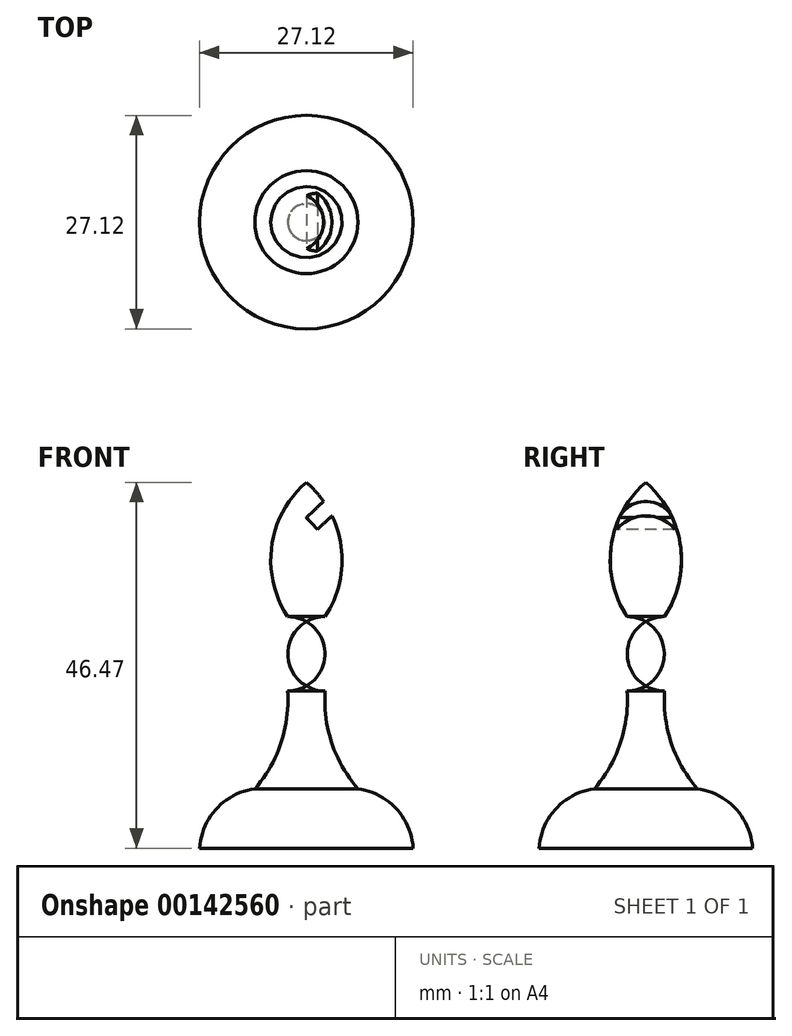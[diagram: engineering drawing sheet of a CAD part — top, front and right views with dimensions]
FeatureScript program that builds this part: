
annotation { "Feature Type Name" : "Feature", "Feature Type Description" : "" }
export const myFeature = defineFeature(function(context is Context, id is Id, definition is map)
    precondition{}
    {
        {
            var Q0;
            Q0=qCreatedBy(makeId("Front.planeOp"),FACE);
            var sketch = newSketch(context, id + "F0", { "sketchPlane" : qUnion([Q0])});
            skArc(sketch, "E0", {"start": v(13.56, 0) * mm, "mid": v(11.4, 5.02) * mm, "end": v(6.54, 7.54) * mm});
            skArc(sketch, "E1", {"start": v(2.38, 19.95) * mm, "mid": v(3.23, 13.33) * mm, "end": v(6.54, 7.54) * mm});
            skArc(sketch, "E2", {"start": v(2.38, 19.95) * mm, "mid": v(7.12, 24.69) * mm, "end": v(2.38, 29.42) * mm});
            skArc(sketch, "E3", {"start": v(2.38, 29.42) * mm, "mid": v(4.4, 38.4) * mm, "end": v(0, 46.47) * mm});
            skLineSegment(sketch, "E4", {"start": v(0, 46.47) * mm, "end": v(0, 0) * mm});
            skArc(sketch, "E5.MirrorCS", {"start": v(-2.38, 29.42) * mm, "mid": v(-4.4, 38.4) * mm, "end": v(0, 46.47) * mm});
            skArc(sketch, "E6.MirrorCS", {"start": v(-2.38, 19.95) * mm, "mid": v(-7.12, 24.69) * mm, "end": v(-2.38, 29.42) * mm});
            skArc(sketch, "E7.MirrorCS", {"start": v(-2.38, 19.95) * mm, "mid": v(-3.23, 13.33) * mm, "end": v(-6.54, 7.54) * mm});
            skArc(sketch, "E8.MirrorCS", {"start": v(-13.56, 0) * mm, "mid": v(-11.4, 5.02) * mm, "end": v(-6.54, 7.54) * mm});
            skLineSegment(sketch, "E9", {"start": v(13.56, 0) * mm, "end": v(-13.56, 0) * mm});
            skPoint(sketch, "E10.endSnap0", {"position": v(4.4, 38.4) * mm});
            skSolve(sketch);
        }
        {
            var Q0;
            Q0=qCreatedBy(makeId("Front.planeOp"),FACE);
            var sketch = newSketch(context, id + "F1", { "sketchPlane" : qUnion([Q0])});
            skLineSegment(sketch, "E11", {"start": v(4.87, 43.76) * mm, "end": v(1.42, 40.5) * mm});
            skLineSegment(sketch, "E12", {"start": v(1.42, 40.5) * mm, "end": v(0, 42) * mm});
            skLineSegment(sketch, "E13", {"start": v(0, 42) * mm, "end": v(3.27, 45.08) * mm});
            skLineSegment(sketch, "E14", {"start": v(3.27, 45.08) * mm, "end": v(4.87, 43.76) * mm});
            skSolve(sketch);
        }
        {
            var Q0;
            {var subQ0=sQuery(id+"F0.wireOp",EDGE,"E4");Q0=makeQuery(id+"F0.imprint","IMPRINT",FACE,{"disambiguationData":[TD([[makeQuery(id+"F0.imprint","IMPRINT",EDGE,{"derivedFrom":subQ0}),-1.0]])]});}
            var Q1;
            Q1=sQuery(id+"F0.wireOp",EDGE,"E4");
            revolve(context, id + "F2", {"entities" : qUnion([Q0]), "axis" : qUnion([Q1]), "revolveType" : RevolveType.FULL});
        }
        {
            var Q0;
            Q0 = qSketchRegion(id + "F1", true);
            extrude(context, id + "F3", {"entities" : qUnion([Q0]), "operationType" : NewBodyOperationType.REMOVE, "endBound" : BoundingType.SYMMETRIC, "oppositeDirection" : true, "depth" : 25.4 * mm});
        }
    });
